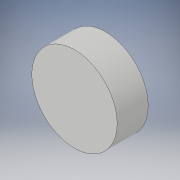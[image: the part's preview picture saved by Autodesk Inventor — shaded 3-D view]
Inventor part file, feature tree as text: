
AUTODESK INVENTOR PART (.ipt)
format: ipt  version: 2018 (Build 220112000, 112)  size: 90,112 bytes
history: native  units: in
note: dims shown in document units (in); Inventor stores cm internally (conversion verified against a paired STEP export)
features: extrude x1, sketch x1
ambient origin geometry x8: Origin, YZ Plane, XZ Plane, XY Plane, X Axis, Y Axis, Z Axis, Center Point
bodies: Solid1 (feature_tree)
feature tree (2):
  extrude  "Extrusion1"  Depth=1.0in TaperAngle=0.0deg
  sketch  "Sketch1"  dims[d0=2.75in d1=1.0in d2=0.0in]
